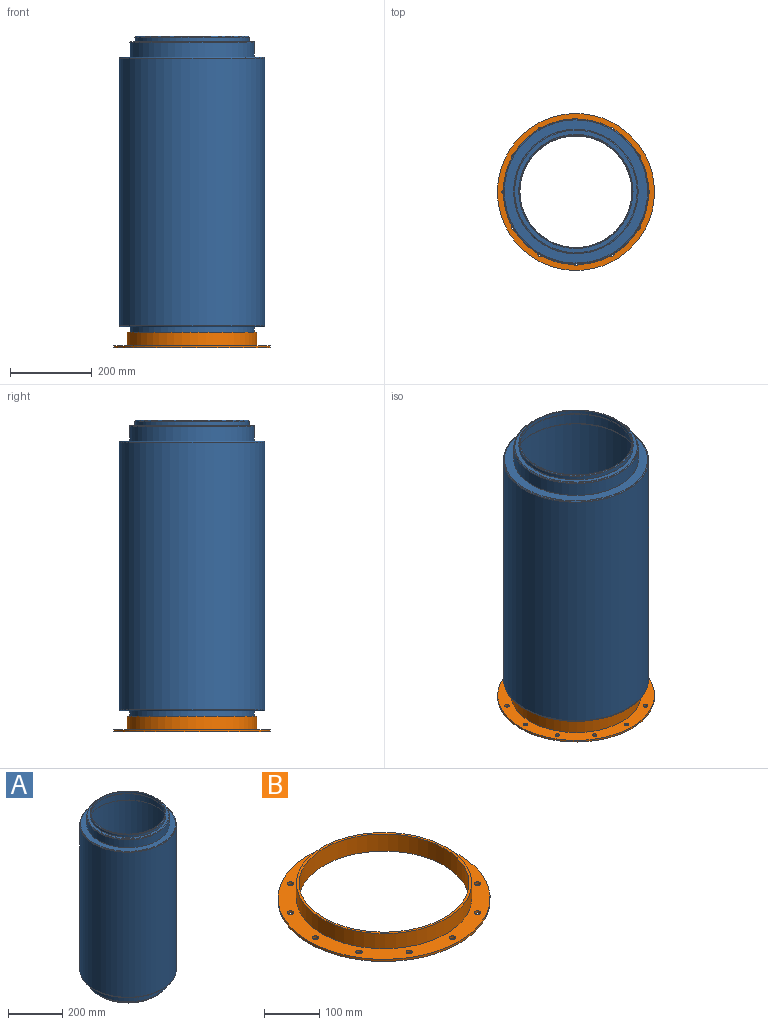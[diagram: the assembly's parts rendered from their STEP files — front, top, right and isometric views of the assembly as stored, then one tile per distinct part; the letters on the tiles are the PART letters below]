
ASSEMBLY  parts=2 mates=1
PART A: 32 faces, bbox 384.9x384.9x762 mm
  f0: cylinder r=152.4mm len=304.8mm, axis (0,0,1), area 34050.7mm2, adj f2,f6
  f1: cylinder r=177.8mm len=655.32mm, axis (0,0,-1), area 732091mm2, adj f7,f23
  f2: plane 350.52x350.52mm, normal (0,0,1), area 23531.5mm2, adj f0,f7
  f3: cylinder r=139.7mm len=279.4mm, axis (0,0,1), area 8918.1mm2, adj f4,f5
  f4: plane 299.72x299.72mm, normal (0,0,1), area 9242.3mm2, adj f3,f6
  f5: torus R=137.16mm, axis (0,0,1), area 3479mm2, adj f3,f8
  f6: torus R=149.86mm, axis (0,0,1), area 3797.3mm2, adj f0,f4
  f7: torus R=175.26mm, axis (0,0,1), area 4434.1mm2, adj f1,f2
  f8: cylinder r=137.16mm len=274.32mm, axis (0,0,1), area 523.2mm2, adj f5,f14
  f9: cylinder r=151.79mm len=303.59mm, axis (0,0,1), area 34494.1mm2, adj f11,f15
  f10: cylinder r=177.19mm len=655.32mm, axis (0,0,-1), area 729591.4mm2, adj f16,f31
  f11: plane 350.52x350.52mm, normal (0,0,-1), area 24111.6mm2, adj f9,f16
  f12: cylinder r=139.09mm len=278.19mm, axis (0,0,1), area 9409.8mm2, adj f13,f14
  f13: plane 299.72x299.72mm, normal (0,0,-1), area 9774mm2, adj f12,f15
  f14: torus R=137.16mm, axis (0,0,1), area 2640.1mm2, adj f8,f12
  f15: torus R=149.86mm, axis (0,0,1), area 2882.4mm2, adj f9,f13
  f16: torus R=175.26mm, axis (0,0,1), area 3367mm2, adj f10,f11
  f17: cylinder r=152.4mm len=304.8mm, axis (0,0,-1), area 34050.7mm2, adj f18,f22
  f18: plane 350.52x350.52mm, normal (0,0,-1), area 23531.5mm2, adj f17,f23
  f19: cylinder r=139.7mm len=279.4mm, axis (0,0,-1), area 8918.1mm2, adj f20,f21
  f20: plane 299.72x299.72mm, normal (0,0,-1), area 9242.3mm2, adj f19,f22
  f21: torus R=137.16mm, axis (0,0,-1), area 3479mm2, adj f19,f24
  f22: torus R=149.86mm, axis (0,0,-1), area 3797.3mm2, adj f17,f20
  f23: torus R=175.26mm, axis (0,0,-1), area 4434.1mm2, adj f1,f18
  f24: cylinder r=137.16mm len=274.32mm, axis (0,0,-1), area 523.2mm2, adj f21,f29
  f25: cylinder r=151.79mm len=303.59mm, axis (0,0,-1), area 34494.1mm2, adj f26,f30
  f26: plane 350.52x350.52mm, normal (0,0,1), area 24111.6mm2, adj f25,f31
  f27: cylinder r=139.09mm len=278.19mm, axis (0,0,-1), area 9409.8mm2, adj f28,f29
  f28: plane 299.72x299.72mm, normal (0,0,1), area 9774mm2, adj f27,f30
  f29: torus R=137.16mm, axis (0,0,-1), area 2640.1mm2, adj f24,f27
  f30: torus R=149.86mm, axis (0,0,-1), area 2882.4mm2, adj f25,f28
  f31: torus R=175.26mm, axis (0,0,-1), area 3367mm2, adj f10,f26
PART B: 18 faces, bbox 384.2x384.2x38.1 mm
  f0: cylinder r=5.56mm len=11.11mm, axis (0,0,-1), area 166.3mm2, adj f14,f16
  f1: cylinder r=5.56mm len=11.11mm, axis (0,0,-1), area 166.3mm2, adj f14,f16
  f2: cylinder r=5.56mm len=11.11mm, axis (0,0,-1), area 166.3mm2, adj f14,f16
  f3: cylinder r=5.56mm len=11.11mm, axis (0,0,-1), area 166.3mm2, adj f14,f16
  f4: cylinder r=5.56mm len=11.11mm, axis (0,0,-1), area 166.3mm2, adj f14,f16
  f5: cylinder r=5.56mm len=11.11mm, axis (0,0,-1), area 166.3mm2, adj f14,f16
  f6: cylinder r=5.56mm len=11.11mm, axis (0,0,-1), area 166.3mm2, adj f14,f16
  f7: cylinder r=5.56mm len=11.11mm, axis (0,0,-1), area 166.3mm2, adj f14,f16
  f8: cylinder r=5.56mm len=11.11mm, axis (0,0,-1), area 166.3mm2, adj f14,f16
  f9: cylinder r=5.56mm len=11.11mm, axis (0,0,-1), area 166.3mm2, adj f14,f16
  f10: cylinder r=5.56mm len=11.11mm, axis (0,0,-1), area 166.3mm2, adj f14,f16
  f11: plane 317.5x317.5mm, normal (0,0,1), area 4679.1mm2, adj f13,f15
  f12: cylinder r=192.09mm len=384.18mm, axis (0,0,-1), area 5748mm2, adj f14,f16
  f13: cylinder r=153.99mm len=307.98mm, axis (0,0,-1), area 36863mm2, adj f11,f14
  f14: plane 384.18x384.18mm, normal (0,0,-1), area 40259.5mm2, adj f0,f1,f2,f3,f4,f5,f6,f7
  f15: cylinder r=158.75mm len=317.5mm, axis (0,0,-1), area 33252.7mm2, adj f11,f16
  f16: plane 384.18x384.18mm, normal (0,0,1), area 35580.4mm2, adj f0,f1,f2,f3,f4,f5,f6,f7
  f17: cylinder r=5.56mm len=11.11mm, axis (0,0,-1), area 166.3mm2, adj f14,f16
PLACE A t=(-561.28,73.77,380.27)mm
PLACE B t=(949.52,236.34,-0.73)mm
MATE fastened B.f13 <-> A.f0  axis (0,0,-1) through (949.52,236.34,-0.73)mm
